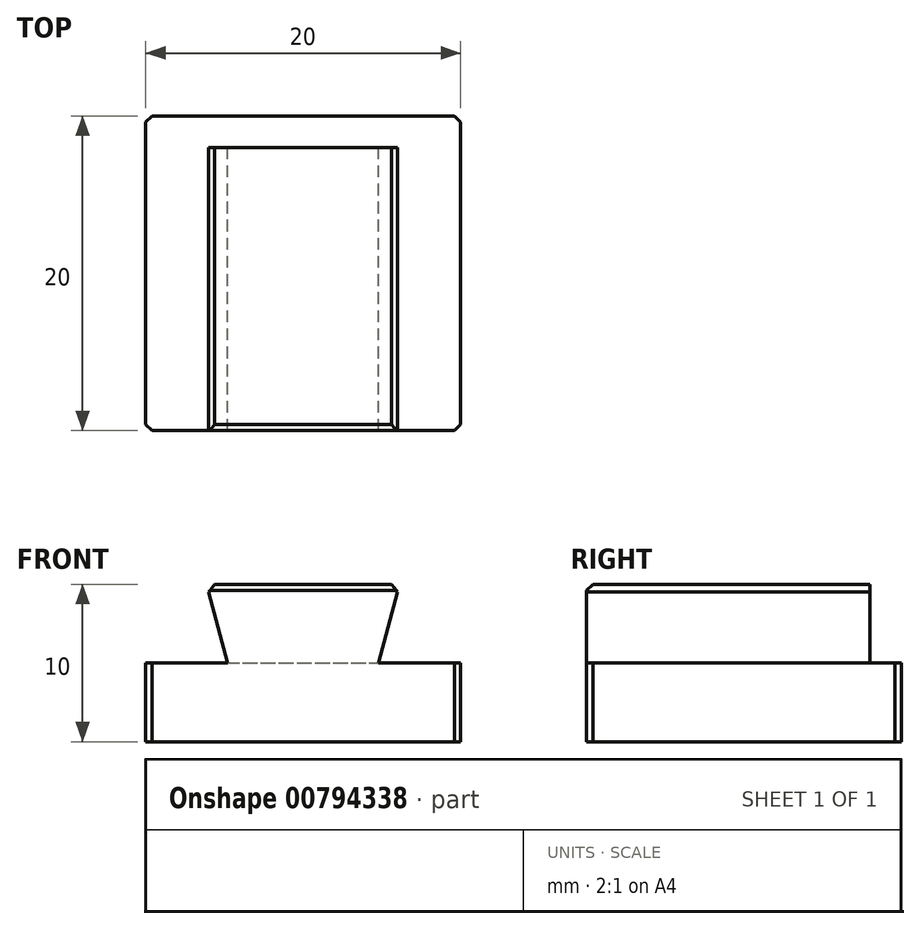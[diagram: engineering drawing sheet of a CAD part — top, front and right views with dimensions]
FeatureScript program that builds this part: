
annotation { "Feature Type Name" : "Feature", "Feature Type Description" : "" }
export const myFeature = defineFeature(function(context is Context, id is Id, definition is map)
    precondition{}
    {
        {
            assignVariable(context, id + "F0", {"name" : "PrintOffset", "anyValue" : 0.4});
        }
        {
            assignVariable(context, id + "F1", {"name" : "DovetailBackstopDepth", "anyValue" : 2});
        }
        {
            assignVariable(context, id + "F2", {"name" : "DovetailDepth", "anyValue" : 20});
        }
        {
            var Q0;
            Q0=qCreatedBy(makeId("Front.planeOp"),FACE);
            var sketch = newSketch(context, id + "F3", { "sketchPlane" : qUnion([Q0])});
            skLineSegment(sketch, "E0", {"start": v(-10, 0) * mm, "end": v(10, 0) * mm});
            skLineSegment(sketch, "E1", {"start": v(-10, 0) * mm, "end": v(-10, 10) * mm});
            skLineSegment(sketch, "E2", {"start": v(10, 10) * mm, "end": v(10, 0) * mm});
            skLineSegment(sketch, "E3", {"start": v(-10, 5) * mm, "end": v(10, 5) * mm});
            skLineSegment(sketch, "E4", {"start": v(-10, 10) * mm, "end": v(10, 10) * mm});
            skLineSegment(sketch, "E5", {"start": v(-6.14, 10) * mm, "end": v(-4.8, 5) * mm});
            skLineSegment(sketch, "E6", {"start": v(0, 0) * mm, "end": v(0, 10) * mm, "construction": true});
            skLineSegment(sketch, "E7.MirrorCS", {"start": v(6.14, 10) * mm, "end": v(4.8, 5) * mm});
            skSolve(sketch);
        }
        {
            var Q0;
            Q0=makeQuery(id+"F3.imprint","IMPRINT",FACE,{"disambiguationData":[TD([[makeQuery(id+"F3.imprint","IMPRINT",EDGE,{"derivedFrom":sQuery(id+"F3.wireOp",EDGE,"E0")}),1.0]])]});
            var Q1;
            {var subQ0=sQuery(id+"F3.wireOp",EDGE,"E5");Q1=makeQuery(id+"F3.imprint","IMPRINT",FACE,{"disambiguationData":[TD([[makeQuery(id+"F3.imprint","IMPRINT",EDGE,{"derivedFrom":subQ0}),1.0]])]});}
            extrude(context, id + "F4", {"entities" : qUnion([Q0, Q1]), "depth" : (getVariable(context, 'DovetailDepth')) * mm, "offsetDistance" : 25 * mm});
        }
        {
            var Q0;
            {var subQ0=sQuery(id+"F3.wireOp",EDGE,"E5");Q0=makeQuery(id+"F3.imprint","IMPRINT",FACE,{"disambiguationData":[TD([[makeQuery(id+"F3.imprint","IMPRINT",EDGE,{"derivedFrom":subQ0}),1.0]])]});}
            extrude(context, id + "F5", {"entities" : qUnion([Q0]), "operationType" : NewBodyOperationType.REMOVE, "depth" : (getVariable(context, 'DovetailBackstopDepth')) * mm, "offsetDistance" : 25 * mm});
        }
        {
            var Q0;
            Q0=makeQuery(id+"F4.opExtrude","SWEPT_EDGE",EDGE,{"disambiguationData":[OSD([sQuery(id+"F3.wireOp",EDGE,"E4"),sQuery(id+"F3.wireOp",EDGE,"E7.MirrorCS")])]});
            var Q1;
            Q1=makeQuery(id+"F4.opExtrude","SWEPT_EDGE",EDGE,{"disambiguationData":[OSD([sQuery(id+"F3.wireOp",EDGE,"E4"),sQuery(id+"F3.wireOp",EDGE,"E5")])]});
            var Q2;
            Q2=makeQuery(id+"F4.opExtrude","CAP_EDGE",EDGE,{"disambiguationData":[OSD([sQuery(id+"F3.wireOp",EDGE,"E4")])],"isStart":false});
            var Q3;
            Q3=makeQuery(id+"F5.boolean.opBoolean","COPY",EDGE,{"derivedFrom":makeQuery(id+"F5.opExtrude","CAP_EDGE",EDGE,{"disambiguationData":[OSD([sQuery(id+"F3.wireOp",EDGE,"E4")])],"isStart":false})});
            var Q4;
            Q4=makeQuery(id+"F4.opExtrude","CAP_EDGE",EDGE,{"disambiguationData":[OSD([sQuery(id+"F3.wireOp",EDGE,"E2")])],"isStart":false});
            var Q5;
            Q5=makeQuery(id+"F4.opExtrude","CAP_EDGE",EDGE,{"disambiguationData":[OSD([sQuery(id+"F3.wireOp",EDGE,"E2")])],"isStart":true});
            var Q6;
            Q6=makeQuery(id+"F4.opExtrude","CAP_EDGE",EDGE,{"disambiguationData":[OSD([sQuery(id+"F3.wireOp",EDGE,"E1")])],"isStart":false});
            var Q7;
            Q7=makeQuery(id+"F4.opExtrude","CAP_EDGE",EDGE,{"disambiguationData":[OSD([sQuery(id+"F3.wireOp",EDGE,"E1")])],"isStart":true});
            chamfer(context, id + "F6", {"entities" : qUnion([Q0, Q1, Q2, Q3, Q4, Q5, Q6, Q7]), "width" : (getVariable(context, 'PrintOffset')) * mm, "tangentPropagation" : true});
        }
    });
